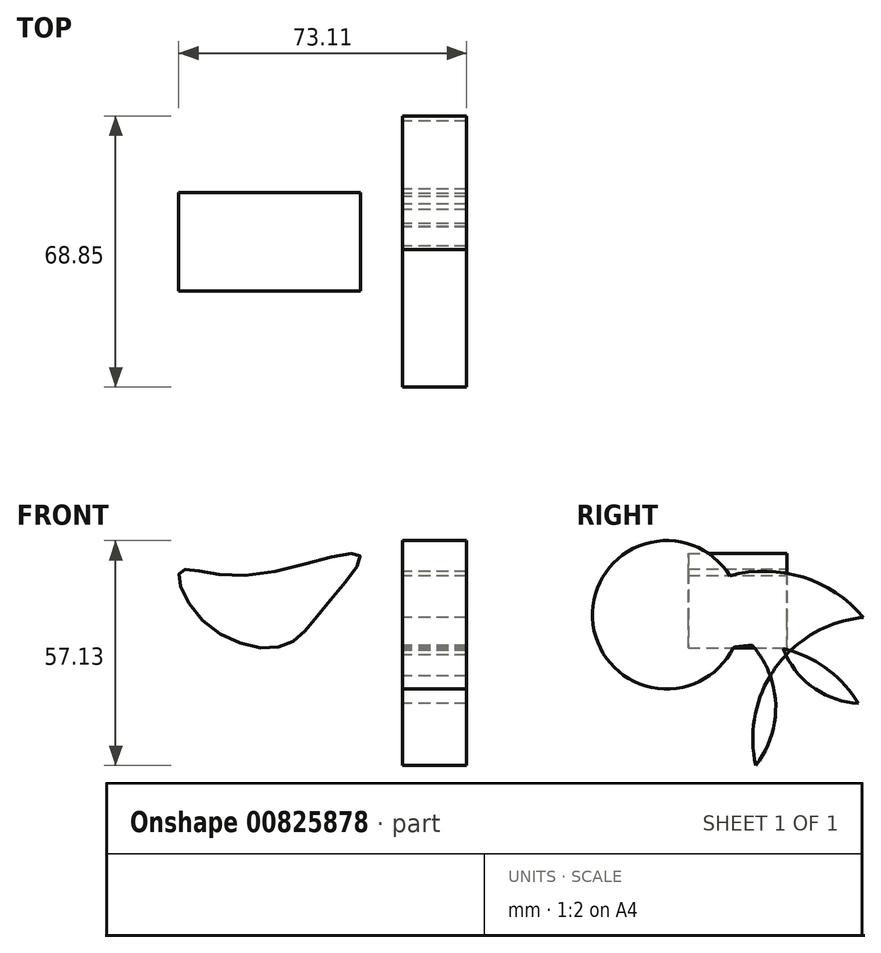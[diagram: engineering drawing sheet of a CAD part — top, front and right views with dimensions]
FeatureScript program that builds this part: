
annotation { "Feature Type Name" : "Feature", "Feature Type Description" : "" }
export const myFeature = defineFeature(function(context is Context, id is Id, definition is map)
    precondition{}
    {
        {
            var Q0;
            Q0=qCreatedBy(makeId("Right.planeOp"),FACE);
            var sketch = newSketch(context, id + "F0", { "sketchPlane" : qUnion([Q0])});
            skCircle(sketch, "E0", {"center": v(-30.5, 49.58) * mm, "radius": 18.86 * mm});
            skCircle(sketch, "E1", {"center": v(-7.88, 11.32) * mm, "radius": 30.47 * mm});
            skCircle(sketch, "E2", {"center": v(19.5, 48.92) * mm, "radius": 21.9 * mm});
            skArc(sketch, "E3", {"start": v(19.5, 48.92) * mm, "mid": v(-5.35, 60.65) * mm, "end": v(-30.5, 49.58) * mm});
            skArc(sketch, "E4", {"start": v(19.5, 48.92) * mm, "mid": v(-2.72, 36.32) * mm, "end": v(-7.88, 11.32) * mm});
            skArc(sketch, "E5", {"start": v(-7.88, 11.32) * mm, "mid": v(-6.12, 38.17) * mm, "end": v(-30.5, 49.58) * mm});
            skSolve(sketch);
        }
        {
            var Q0;
            {var subQ0=sQuery(id+"F0.wireOp",EDGE,"E3");var subQ1=sQuery(id+"F0.wireOp",EDGE,"E0");var subQ2=makeQuery(id+"F0.imprint","INTERSECT",VERTEX,{"derivedFrom":[subQ1,subQ0]});Q0=makeQuery(id+"F0.imprint","IMPRINT",FACE,{"disambiguationData":[TD([[makeQuery(id+"F0.imprint","IMPRINT",EDGE,{"disambiguationData":[TD([[subQ2,1.0]])],"derivedFrom":subQ1}),-1.0]])]});}
            var Q1;
            {var subQ3=sQuery(id+"F0.wireOp",EDGE,"E0");var subQ5=sQuery(id+"F0.wireOp",EDGE,"E1");var subQ6=makeQuery(id+"F0.imprint","INTERSECT",VERTEX,{"disambiguationData":[OD(0.0)],"derivedFrom":[subQ3,subQ5]});Q1=makeQuery(id+"F0.imprint","IMPRINT",FACE,{"disambiguationData":[TD([[makeQuery(id+"F0.imprint","IMPRINT",EDGE,{"disambiguationData":[TD([[subQ6,1.0]])],"derivedFrom":subQ3}),1.0]])]});}
            var Q2;
            {var subQ0=sQuery(id+"F0.wireOp",EDGE,"E4");var subQ1=sQuery(id+"F0.wireOp",EDGE,"E1");var subQ2=makeQuery(id+"F0.imprint","INTERSECT",VERTEX,{"derivedFrom":[subQ1,subQ0]});Q2=makeQuery(id+"F0.imprint","IMPRINT",FACE,{"disambiguationData":[TD([[makeQuery(id+"F0.imprint","IMPRINT",EDGE,{"disambiguationData":[TD([[subQ2,-1.0]])],"derivedFrom":subQ1}),-1.0]])]});}
            var Q3;
            {var subQ0=sQuery(id+"F0.wireOp",EDGE,"E5");var subQ1=sQuery(id+"F0.wireOp",EDGE,"E4");var subQ2=makeQuery(id+"F0.imprint","INTERSECT",VERTEX,{"disambiguationData":[OD(0.0)],"derivedFrom":[subQ1,subQ0]});Q3=makeQuery(id+"F0.imprint","IMPRINT",FACE,{"disambiguationData":[TD([[makeQuery(id+"F0.imprint","IMPRINT",EDGE,{"disambiguationData":[TD([[subQ2,1.0]])],"derivedFrom":subQ1}),1.0]])]});}
            var Q4;
            {var subQ0=sQuery(id+"F0.wireOp",EDGE,"E2");var subQ1=sQuery(id+"F0.wireOp",EDGE,"E1");var subQ2=makeQuery(id+"F0.imprint","INTERSECT",VERTEX,{"disambiguationData":[OD(1.0)],"derivedFrom":[subQ1,subQ0]});Q4=makeQuery(id+"F0.imprint","IMPRINT",FACE,{"disambiguationData":[TD([[makeQuery(id+"F0.imprint","IMPRINT",EDGE,{"disambiguationData":[TD([[subQ2,-1.0]])],"derivedFrom":subQ1}),1.0]])]});}
            var Q5;
            {var subQ0=sQuery(id+"F0.wireOp",EDGE,"E2");var subQ1=sQuery(id+"F0.wireOp",EDGE,"E1");var subQ2=makeQuery(id+"F0.imprint","INTERSECT",VERTEX,{"disambiguationData":[OD(0.0)],"derivedFrom":[subQ1,subQ0]});Q5=makeQuery(id+"F0.imprint","IMPRINT",FACE,{"disambiguationData":[TD([[makeQuery(id+"F0.imprint","IMPRINT",EDGE,{"disambiguationData":[TD([[subQ2,-1.0]])],"derivedFrom":subQ1}),1.0]])]});}
            var Q6;
            {var subQ0=sQuery(id+"F0.wireOp",EDGE,"E1");var subQ1=sQuery(id+"F0.wireOp",EDGE,"E0");var subQ2=makeQuery(id+"F0.imprint","INTERSECT",VERTEX,{"disambiguationData":[OD(0.0)],"derivedFrom":[subQ1,subQ0]});Q6=makeQuery(id+"F0.imprint","IMPRINT",FACE,{"disambiguationData":[TD([[makeQuery(id+"F0.imprint","IMPRINT",EDGE,{"disambiguationData":[TD([[subQ2,-1.0]])],"derivedFrom":subQ1}),1.0]])]});}
            var Q7;
            {var subQ0=sQuery(id+"F0.wireOp",EDGE,"E1");var subQ1=sQuery(id+"F0.wireOp",EDGE,"E0");var subQ2=makeQuery(id+"F0.imprint","INTERSECT",VERTEX,{"disambiguationData":[OD(1.0)],"derivedFrom":[subQ1,subQ0]});Q7=makeQuery(id+"F0.imprint","IMPRINT",FACE,{"disambiguationData":[TD([[makeQuery(id+"F0.imprint","IMPRINT",EDGE,{"disambiguationData":[TD([[subQ2,-1.0]])],"derivedFrom":subQ1}),-1.0]])]});}
            var Q8;
            {var subQ0=sQuery(id+"F0.wireOp",EDGE,"E3");var subQ1=sQuery(id+"F0.wireOp",EDGE,"E0");var subQ2=makeQuery(id+"F0.imprint","INTERSECT",VERTEX,{"derivedFrom":[subQ1,subQ0]});Q8=makeQuery(id+"F0.imprint","IMPRINT",FACE,{"disambiguationData":[TD([[makeQuery(id+"F0.imprint","IMPRINT",EDGE,{"disambiguationData":[TD([[subQ2,1.0]])],"derivedFrom":subQ1}),1.0]])]});}
            extrude(context, id + "F1", {"entities" : qUnion([Q0, Q1, Q2, Q3, Q4, Q5, Q6, Q7, Q8]), "depth" : 16.3 * mm, "offsetDistance" : 25 * mm});
        }
        {
            var Q0;
            Q0=qCreatedBy(makeId("Front.planeOp"),FACE);
            var sketch = newSketch(context, id + "F2", { "sketchPlane" : qUnion([Q0])});
            skFitSpline(sketch, "E6", {"points": [v(-50.78, 48.2) * mm, v(-56.45, 60.58) * mm, v(-41.01, 59.55) * mm, v(-10.86, 64.76) * mm, v(-19.6, 51.72) * mm, v(-31.09, 41.45) * mm, v(-50.78, 48.2) * mm]});
            skSolve(sketch);
        }
        {
            var Q0;
            Q0=makeQuery(id+"F2.imprint","IMPRINT",FACE,{"disambiguationData":[TD([[makeQuery(id+"F2.imprint","IMPRINT",EDGE,{"derivedFrom":sQuery(id+"F2.wireOp",EDGE,"E6")}),-1.0]])]});
            extrude(context, id + "F3", {"entities" : qUnion([Q0]), "depth" : 25 * mm, "offsetDistance" : 25 * mm});
        }
    });
